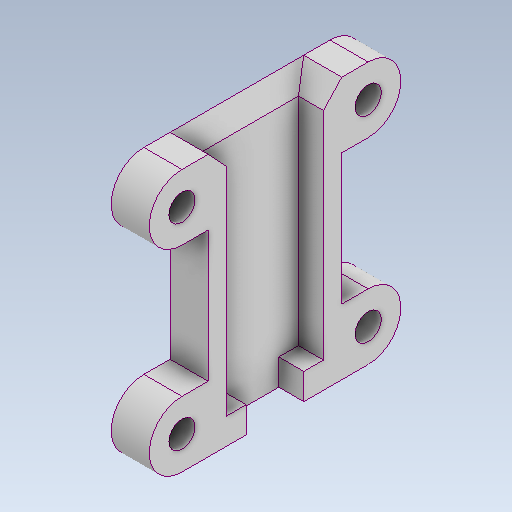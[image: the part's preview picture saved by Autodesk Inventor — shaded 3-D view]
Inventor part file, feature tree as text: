
AUTODESK INVENTOR PART (.ipt)
format: ipt  version: 2020 (Build 240168000, 168)  size: 171,520 bytes
history: native  units: in
note: dims shown in document units (in); Inventor stores cm internally (conversion verified against a paired STEP export)
features: other x3, sketch x3
ambient origin geometry x8: Origin, YZ Plane, XZ Plane, XY Plane, X Axis, Y Axis, Z Axis, Center Point
bodies: Solid1 (feature_tree)
feature tree (6):
  other  "PistonCasingBot.ipt"
  other  "Solid1::PistonCasingBot.ipt"
  other  "TaggingFeature1"
  sketch  "Sketch1"  dims[d0=0.3937in]
  sketch  "Sketch2"
  sketch  "Sketch3"
